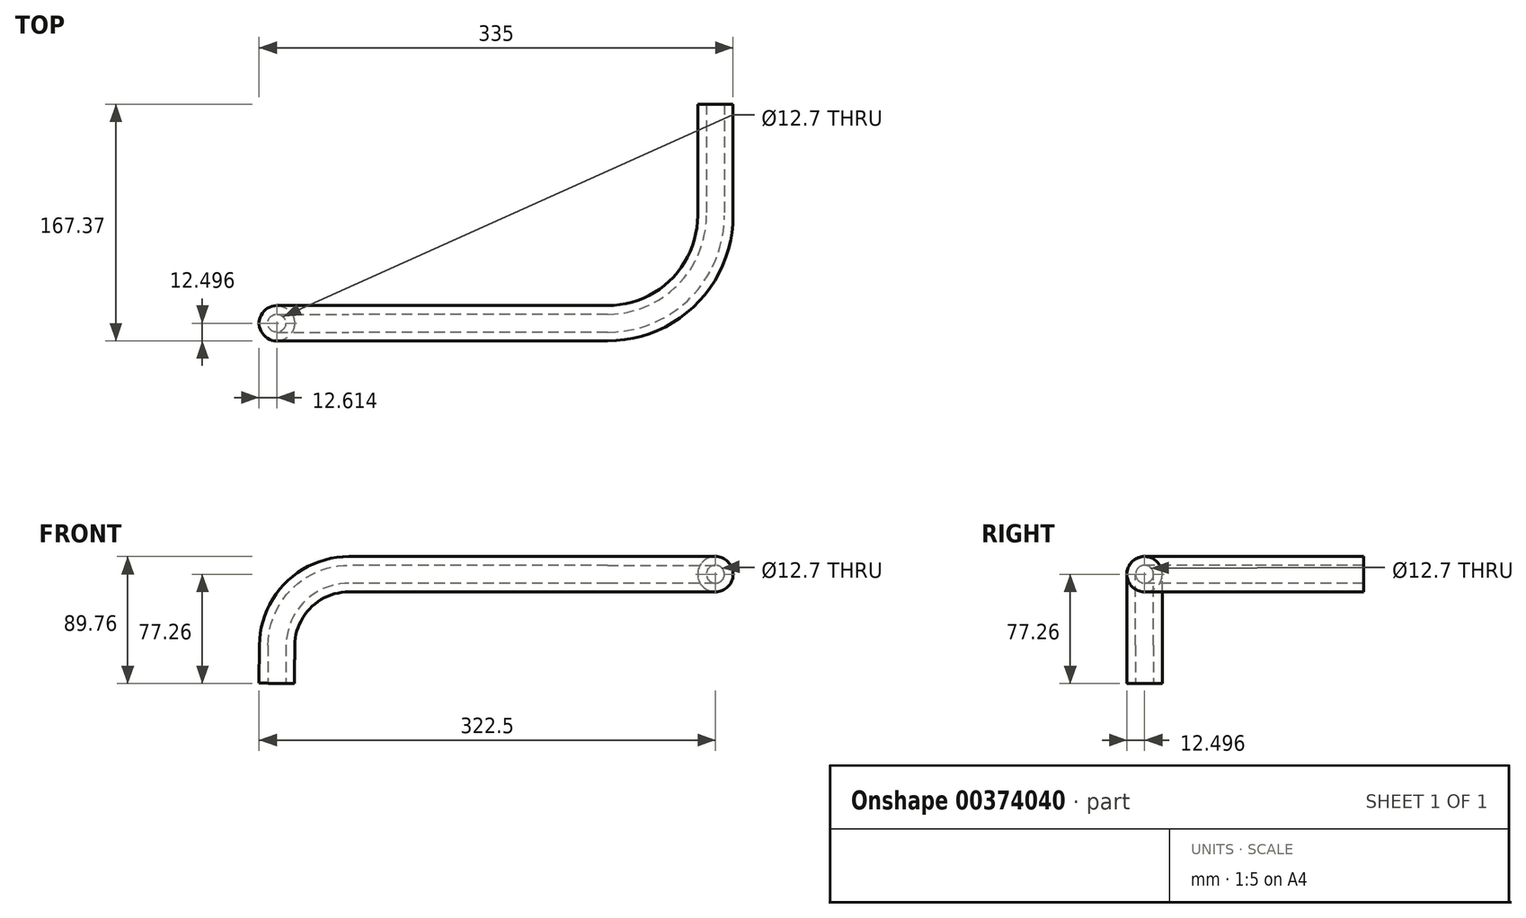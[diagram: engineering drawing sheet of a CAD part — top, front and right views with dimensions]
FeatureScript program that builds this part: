
annotation { "Feature Type Name" : "Feature", "Feature Type Description" : "" }
export const myFeature = defineFeature(function(context is Context, id is Id, definition is map)
    precondition{}
    {
        {
            var Q0;
            Q0=qCreatedBy(makeId("Front.planeOp"),FACE);
            var sketch = newSketch(context, id + "F0", { "sketchPlane" : qUnion([Q0])});
            skCircle(sketch, "E0", {"center": v(0, 0) * mm, "radius": 6.35 * mm});
            skCircle(sketch, "E1", {"center": v(0, 0) * mm, "radius": 12.5 * mm});
            skSolve(sketch);
        }
        {
            var Q0;
            Q0=qCreatedBy(makeId("Top.planeOp"),FACE);
            var sketch = newSketch(context, id + "F1", { "sketchPlane" : qUnion([Q0])});
            skLineSegment(sketch, "E2", {"start": v(0, 0) * mm, "end": v(0, -78.67) * mm});
            skLineSegment(sketch, "E3", {"start": v(-76.2, -154.87) * mm, "end": v(-235.88, -154.87) * mm});
            skPoint(sketch, "E4.visualSharp", {"position": v(0, -154.87) * mm});
            skArc(sketch, "E4.filletArc", {"start": v(-76.2, -154.87) * mm, "mid": v(-22.32, -132.56) * mm, "end": v(0, -78.67) * mm});
            skSolve(sketch);
        }
        {
            var Q0;
            Q0=qCreatedBy(makeId("Front.planeOp"),FACE);
            cPlane(context, id + "F2", {"entities" : qUnion([Q0]), "cplaneType" : CPlaneType.OFFSET, "offset" : 154.87 * mm, "width" : 150 * mm, "height" : 150 * mm});
        }
        {
            var Q0;
            Q0=qCreatedBy(id+"F2.planeOp",FACE);
            var sketch = newSketch(context, id + "F3", { "sketchPlane" : qUnion([Q0])});
            skLineSegment(sketch, "E5", {"start": v(-235.88, 0) * mm, "end": v(-258.98, 0) * mm});
            skLineSegment(sketch, "E6", {"start": v(-310, -77.15) * mm, "end": v(-309.77, -50.37) * mm});
            skPoint(sketch, "E7.newPointA", {"position": v(-309.24, 13.06) * mm});
            skPoint(sketch, "E7.newPointB", {"position": v(-309.24, 0) * mm});
            skArc(sketch, "E7.filletArc", {"start": v(-258.98, 0) * mm, "mid": v(-294.74, -14.73) * mm, "end": v(-309.77, -50.37) * mm});
            skSolve(sketch);
        }
        {
            var Q0;
            Q0 = qSketchRegion(id + "F0", true);
            var Q1;
            Q1 = qConstructionFilter(qBodyType(qCreatedBy(id + "F1" ,EDGE), BodyType.WIRE), ConstructionObject.NO);
            var Q2;
            Q2 = qConstructionFilter(qBodyType(qCreatedBy(id + "F3" ,EDGE), BodyType.WIRE), ConstructionObject.NO);
            sweep(context, id + "F4", {"profiles" : qUnion([Q0]), "path" : qUnion([Q1, Q2])});
        }
    });
